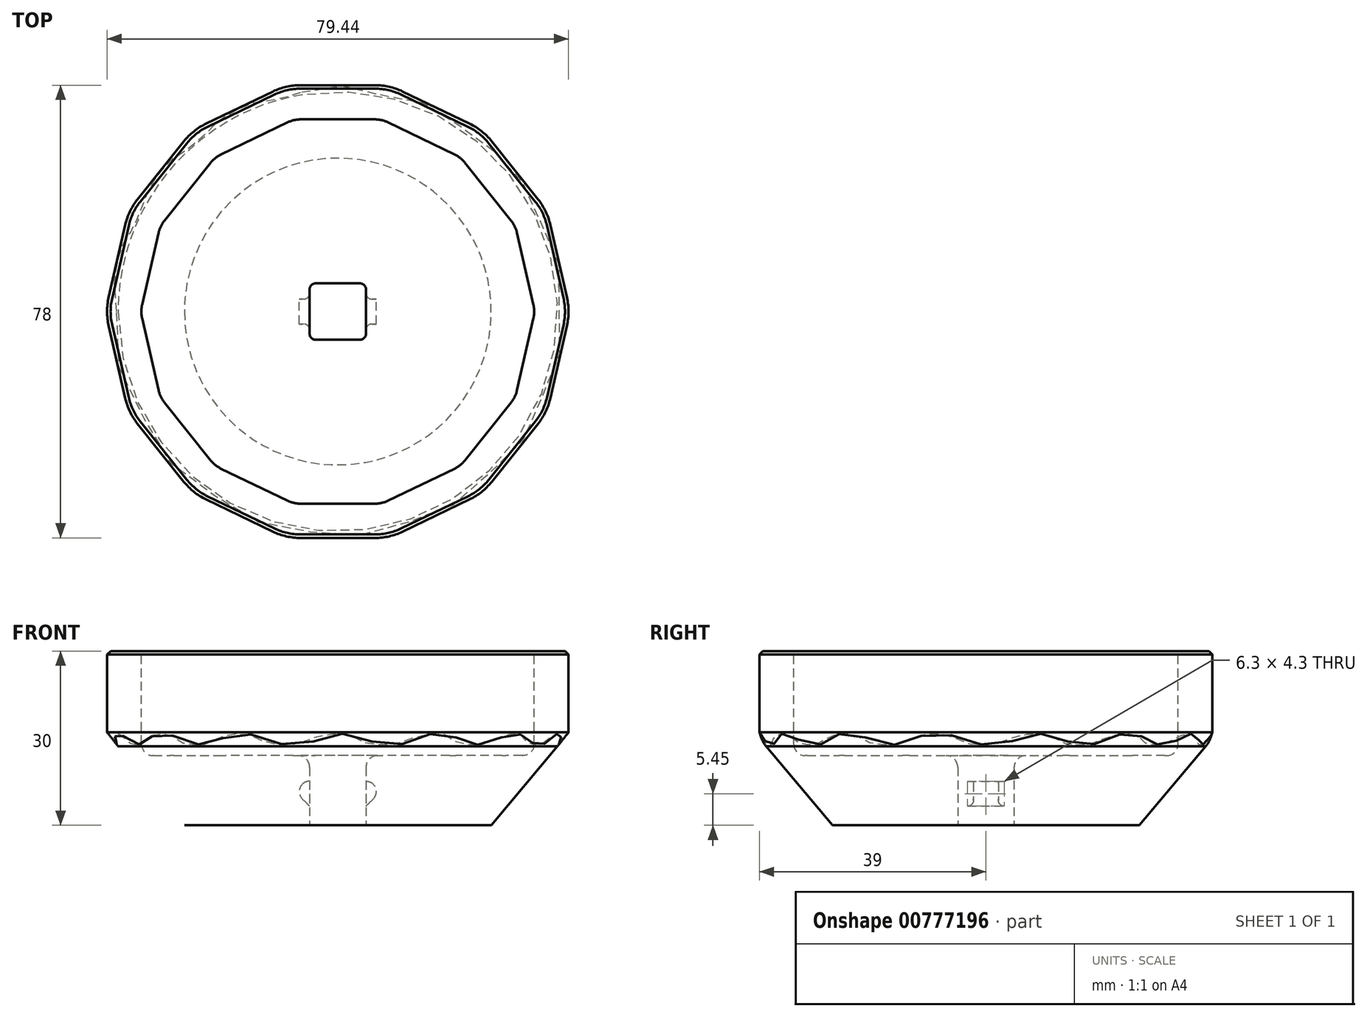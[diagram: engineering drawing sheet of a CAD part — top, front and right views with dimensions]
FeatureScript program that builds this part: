
annotation { "Feature Type Name" : "Feature", "Feature Type Description" : "" }
export const myFeature = defineFeature(function(context is Context, id is Id, definition is map)
    precondition{}
    {
        {
            var Q0;
            Q0=qCreatedBy(makeId("Top.planeOp"),FACE);
            var sketch = newSketch(context, id + "F0", { "sketchPlane" : qUnion([Q0])});
            skLineSegment(sketch, "E0.bottom", {"start": v(3.85, 4.85) * mm, "end": v(-3.85, 4.85) * mm});
            skLineSegment(sketch, "E0.top", {"start": v(3.85, -4.85) * mm, "end": v(-3.85, -4.85) * mm});
            skLineSegment(sketch, "E0.left", {"start": v(4.85, 3.85) * mm, "end": v(4.85, -3.85) * mm});
            skLineSegment(sketch, "E0.right", {"start": v(-4.85, 3.85) * mm, "end": v(-4.85, -3.85) * mm});
            skPoint(sketch, "E0.middle", {"position": v(0, 0) * mm});
            skPoint(sketch, "E1.visualSharp", {"position": v(-4.85, -4.85) * mm});
            skArc(sketch, "E1.filletArc", {"start": v(-4.85, -3.85) * mm, "mid": v(-4.56, -4.56) * mm, "end": v(-3.85, -4.85) * mm});
            skPoint(sketch, "E2.visualSharp", {"position": v(4.85, -4.85) * mm});
            skArc(sketch, "E2.filletArc", {"start": v(3.85, -4.85) * mm, "mid": v(4.56, -4.56) * mm, "end": v(4.85, -3.85) * mm});
            skPoint(sketch, "E3.visualSharp", {"position": v(4.85, 4.85) * mm});
            skArc(sketch, "E3.filletArc", {"start": v(4.85, 3.85) * mm, "mid": v(4.56, 4.56) * mm, "end": v(3.85, 4.85) * mm});
            skPoint(sketch, "E4.visualSharp", {"position": v(-4.85, 4.85) * mm});
            skArc(sketch, "E4.filletArc", {"start": v(-3.85, 4.85) * mm, "mid": v(-4.56, 4.56) * mm, "end": v(-4.85, 3.85) * mm});
            skSolve(sketch);
        }
        {
            var Q0;
            Q0=qCreatedBy(makeId("Front.planeOp"),FACE);
            var sketch = newSketch(context, id + "F1", { "sketchPlane" : qUnion([Q0])});
            skLineSegment(sketch, "E5", {"start": v(0, 0) * mm, "end": v(0, 30) * mm});
            skLineSegment(sketch, "E6", {"start": v(0, 30) * mm, "end": v(-39, 30) * mm});
            skLineSegment(sketch, "E7", {"start": v(-39, 30) * mm, "end": v(-39, 16.82) * mm});
            skLineSegment(sketch, "E8", {"start": v(-37.83, 13.6) * mm, "end": v(-26.41, 0) * mm});
            skLineSegment(sketch, "E9", {"start": v(-26.41, 0) * mm, "end": v(0, 0) * mm});
            skLineSegment(sketch, "E10", {"start": v(0, 0) * mm, "end": v(0, -5.87) * mm, "construction": true});
            skPoint(sketch, "E11.visualSharp", {"position": v(-39, 15) * mm});
            skArc(sketch, "E11.filletArc", {"start": v(-39, 16.82) * mm, "mid": v(-38.7, 15.1) * mm, "end": v(-37.83, 13.6) * mm});
            skSolve(sketch);
        }
        {
            var Q0;
            Q0 = qSketchRegion(id + "F1", true);
            var Q1;
            Q1=sQuery(id+"F1.wireOp",EDGE,"E5");
            revolve(context, id + "F2", {"surfaceOperationType" : NewSurfaceOperationType.NEW, "entities" : qUnion([Q0]), "axis" : qUnion([Q1]), "revolveType" : RevolveType.FULL});
        }
        {
            var Q0;
            Q0 = qSketchRegion(id + "F0", true);
            extrude(context, id + "F3", {"entities" : qUnion([Q0]), "operationType" : NewBodyOperationType.REMOVE, "endBound" : BoundingType.THROUGH_ALL, "depth" : 12 * mm, "offsetDistance" : 25 * mm});
        }
        {
            var Q0;
            Q0=makeQuery(id+"F2.opRevolve","SWEPT_FACE",FACE,{"disambiguationData":[OSD([sQuery(id+"F1.wireOp",EDGE,"E6")])]});
            var sketch = newSketch(context, id + "F4", { "sketchPlane" : qUnion([Q0])});
            skCircle(sketch, "E12.cCircle", {"center": v(0, 0) * mm, "radius": 33.95 * mm, "construction": true});
            skLineSegment(sketch, "E12.0", {"start": v(21.88, 25.65) * mm, "end": v(29.88, 15.62) * mm});
            skLineSegment(sketch, "E12.1", {"start": v(30.84, 13.62) * mm, "end": v(33.7, 1.11) * mm});
            skLineSegment(sketch, "E12.2", {"start": v(33.7, -1.11) * mm, "end": v(30.84, -13.62) * mm});
            skLineSegment(sketch, "E12.3", {"start": v(29.88, -15.62) * mm, "end": v(21.88, -25.65) * mm});
            skLineSegment(sketch, "E12.4", {"start": v(20.14, -27.04) * mm, "end": v(8.58, -32.6) * mm});
            skLineSegment(sketch, "E12.5", {"start": v(6.41, -33.1) * mm, "end": v(-6.41, -33.1) * mm});
            skLineSegment(sketch, "E12.6", {"start": v(-8.58, -32.6) * mm, "end": v(-20.14, -27.04) * mm});
            skLineSegment(sketch, "E12.7", {"start": v(-21.88, -25.65) * mm, "end": v(-29.88, -15.62) * mm});
            skLineSegment(sketch, "E12.8", {"start": v(-30.84, -13.62) * mm, "end": v(-33.7, -1.11) * mm});
            skLineSegment(sketch, "E12.9", {"start": v(-33.7, 1.11) * mm, "end": v(-30.84, 13.62) * mm});
            skLineSegment(sketch, "E12.10", {"start": v(-29.88, 15.62) * mm, "end": v(-21.88, 25.65) * mm});
            skLineSegment(sketch, "E12.11", {"start": v(-20.14, 27.04) * mm, "end": v(-8.58, 32.6) * mm});
            skLineSegment(sketch, "E12.12", {"start": v(-6.41, 33.1) * mm, "end": v(6.41, 33.1) * mm});
            skLineSegment(sketch, "E12.13", {"start": v(8.58, 32.6) * mm, "end": v(20.14, 27.04) * mm});
            skPoint(sketch, "E13.visualSharp", {"position": v(33.95, 0) * mm});
            skArc(sketch, "E13.filletArc", {"start": v(33.7, -1.11) * mm, "mid": v(33.82, 0) * mm, "end": v(33.7, 1.11) * mm});
            skPoint(sketch, "E14.visualSharp", {"position": v(30.59, -14.73) * mm});
            skArc(sketch, "E14.filletArc", {"start": v(29.88, -15.62) * mm, "mid": v(30.47, -14.68) * mm, "end": v(30.84, -13.62) * mm});
            skPoint(sketch, "E15.visualSharp", {"position": v(30.59, 14.73) * mm});
            skArc(sketch, "E15.filletArc", {"start": v(30.84, 13.62) * mm, "mid": v(30.47, 14.68) * mm, "end": v(29.88, 15.62) * mm});
            skPoint(sketch, "E16.visualSharp", {"position": v(21.17, 26.54) * mm});
            skArc(sketch, "E16.filletArc", {"start": v(21.88, 25.65) * mm, "mid": v(21.09, 26.44) * mm, "end": v(20.14, 27.04) * mm});
            skPoint(sketch, "E17.visualSharp", {"position": v(7.55, 33.1) * mm});
            skArc(sketch, "E17.filletArc", {"start": v(8.58, 32.6) * mm, "mid": v(7.53, 32.97) * mm, "end": v(6.41, 33.1) * mm});
            skPoint(sketch, "E18.visualSharp", {"position": v(-7.55, 33.1) * mm});
            skArc(sketch, "E18.filletArc", {"start": v(-6.41, 33.1) * mm, "mid": v(-7.53, 32.97) * mm, "end": v(-8.58, 32.6) * mm});
            skPoint(sketch, "E19.visualSharp", {"position": v(-21.17, 26.54) * mm});
            skArc(sketch, "E19.filletArc", {"start": v(-20.14, 27.04) * mm, "mid": v(-21.09, 26.44) * mm, "end": v(-21.88, 25.65) * mm});
            skPoint(sketch, "E20.visualSharp", {"position": v(-30.59, 14.73) * mm});
            skArc(sketch, "E20.filletArc", {"start": v(-29.88, 15.62) * mm, "mid": v(-30.47, 14.68) * mm, "end": v(-30.84, 13.62) * mm});
            skPoint(sketch, "E21.visualSharp", {"position": v(-33.95, 0) * mm});
            skArc(sketch, "E21.filletArc", {"start": v(-33.7, 1.11) * mm, "mid": v(-33.82, 0) * mm, "end": v(-33.7, -1.11) * mm});
            skPoint(sketch, "E22.visualSharp", {"position": v(-30.59, -14.73) * mm});
            skArc(sketch, "E22.filletArc", {"start": v(-30.84, -13.62) * mm, "mid": v(-30.47, -14.68) * mm, "end": v(-29.88, -15.62) * mm});
            skPoint(sketch, "E23.visualSharp", {"position": v(-21.17, -26.54) * mm});
            skArc(sketch, "E23.filletArc", {"start": v(-21.88, -25.65) * mm, "mid": v(-21.09, -26.44) * mm, "end": v(-20.14, -27.04) * mm});
            skPoint(sketch, "E24.visualSharp", {"position": v(-7.55, -33.1) * mm});
            skArc(sketch, "E24.filletArc", {"start": v(-8.58, -32.6) * mm, "mid": v(-7.53, -32.97) * mm, "end": v(-6.41, -33.1) * mm});
            skPoint(sketch, "E25.visualSharp", {"position": v(7.55, -33.1) * mm});
            skArc(sketch, "E25.filletArc", {"start": v(6.41, -33.1) * mm, "mid": v(7.53, -32.97) * mm, "end": v(8.58, -32.6) * mm});
            skPoint(sketch, "E26.visualSharp", {"position": v(21.17, -26.54) * mm});
            skArc(sketch, "E26.filletArc", {"start": v(20.14, -27.04) * mm, "mid": v(21.09, -26.44) * mm, "end": v(21.88, -25.65) * mm});
            skSolve(sketch);
        }
        {
            var Q0;
            Q0=makeQuery(id+"F4.imprint","IMPRINT",FACE,{"disambiguationData":[TD([[makeQuery(id+"F4.imprint","IMPRINT",EDGE,{"derivedFrom":sQuery(id+"F4.wireOp",EDGE,"E12.0")}),1.0]])]});
            var sketch = newSketch(context, id + "F5", { "sketchPlane" : qUnion([Q0])});
            skCircle(sketch, "E27.0", {"center": v(0, 0) * mm, "radius": 33.95 * mm, "construction": true});
            skLineSegment(sketch, "E27.1", {"start": v(21.88, 25.65) * mm, "end": v(29.88, 15.62) * mm});
            skLineSegment(sketch, "E27.2", {"start": v(30.84, 13.62) * mm, "end": v(33.7, 1.11) * mm});
            skLineSegment(sketch, "E27.3", {"start": v(33.7, -1.11) * mm, "end": v(30.84, -13.62) * mm});
            skLineSegment(sketch, "E27.4", {"start": v(29.88, -15.62) * mm, "end": v(21.88, -25.65) * mm});
            skLineSegment(sketch, "E27.5", {"start": v(20.14, -27.04) * mm, "end": v(8.58, -32.6) * mm});
            skLineSegment(sketch, "E27.6", {"start": v(6.41, -33.1) * mm, "end": v(-6.41, -33.1) * mm});
            skLineSegment(sketch, "E27.7", {"start": v(-8.58, -32.6) * mm, "end": v(-20.14, -27.04) * mm});
            skLineSegment(sketch, "E27.8", {"start": v(-21.88, -25.65) * mm, "end": v(-29.88, -15.62) * mm});
            skLineSegment(sketch, "E27.9", {"start": v(-30.84, -13.62) * mm, "end": v(-33.7, -1.11) * mm});
            skLineSegment(sketch, "E27.10", {"start": v(-33.7, 1.11) * mm, "end": v(-30.84, 13.62) * mm});
            skLineSegment(sketch, "E27.11", {"start": v(-29.88, 15.62) * mm, "end": v(-21.88, 25.65) * mm});
            skLineSegment(sketch, "E27.12", {"start": v(-20.14, 27.04) * mm, "end": v(-8.58, 32.6) * mm});
            skLineSegment(sketch, "E27.13", {"start": v(-6.41, 33.1) * mm, "end": v(6.41, 33.1) * mm});
            skLineSegment(sketch, "E27.14", {"start": v(8.58, 32.6) * mm, "end": v(20.14, 27.04) * mm});
            skPoint(sketch, "E27.15", {"position": v(33.95, 0) * mm});
            skArc(sketch, "E27.16", {"start": v(33.7, -1.11) * mm, "mid": v(33.82, 0) * mm, "end": v(33.7, 1.11) * mm});
            skPoint(sketch, "E27.17", {"position": v(30.59, -14.73) * mm});
            skArc(sketch, "E27.18", {"start": v(29.88, -15.62) * mm, "mid": v(30.47, -14.68) * mm, "end": v(30.84, -13.62) * mm});
            skPoint(sketch, "E27.19", {"position": v(30.59, 14.73) * mm});
            skArc(sketch, "E27.20", {"start": v(30.84, 13.62) * mm, "mid": v(30.47, 14.68) * mm, "end": v(29.88, 15.62) * mm});
            skPoint(sketch, "E27.21", {"position": v(21.17, 26.54) * mm});
            skArc(sketch, "E27.22", {"start": v(21.88, 25.65) * mm, "mid": v(21.09, 26.44) * mm, "end": v(20.14, 27.04) * mm});
            skPoint(sketch, "E27.23", {"position": v(7.55, 33.1) * mm});
            skArc(sketch, "E27.24", {"start": v(8.58, 32.6) * mm, "mid": v(7.53, 32.97) * mm, "end": v(6.41, 33.1) * mm});
            skPoint(sketch, "E27.25", {"position": v(-7.55, 33.1) * mm});
            skArc(sketch, "E27.26", {"start": v(-6.41, 33.1) * mm, "mid": v(-7.53, 32.97) * mm, "end": v(-8.58, 32.6) * mm});
            skPoint(sketch, "E27.27", {"position": v(-21.17, 26.54) * mm});
            skArc(sketch, "E27.28", {"start": v(-20.14, 27.04) * mm, "mid": v(-21.09, 26.44) * mm, "end": v(-21.88, 25.65) * mm});
            skPoint(sketch, "E27.29", {"position": v(-30.59, 14.73) * mm});
            skArc(sketch, "E27.30", {"start": v(-29.88, 15.62) * mm, "mid": v(-30.47, 14.68) * mm, "end": v(-30.84, 13.62) * mm});
            skPoint(sketch, "E27.31", {"position": v(-33.95, 0) * mm});
            skArc(sketch, "E27.32", {"start": v(-33.7, 1.11) * mm, "mid": v(-33.82, 0) * mm, "end": v(-33.7, -1.11) * mm});
            skPoint(sketch, "E27.33", {"position": v(-30.59, -14.73) * mm});
            skArc(sketch, "E27.34", {"start": v(-30.84, -13.62) * mm, "mid": v(-30.47, -14.68) * mm, "end": v(-29.88, -15.62) * mm});
            skPoint(sketch, "E27.35", {"position": v(-21.17, -26.54) * mm});
            skArc(sketch, "E27.36", {"start": v(-21.88, -25.65) * mm, "mid": v(-21.09, -26.44) * mm, "end": v(-20.14, -27.04) * mm});
            skPoint(sketch, "E27.37", {"position": v(-7.55, -33.1) * mm});
            skArc(sketch, "E27.38", {"start": v(-8.58, -32.6) * mm, "mid": v(-7.53, -32.97) * mm, "end": v(-6.41, -33.1) * mm});
            skPoint(sketch, "E27.39", {"position": v(7.55, -33.1) * mm});
            skArc(sketch, "E27.40", {"start": v(6.41, -33.1) * mm, "mid": v(7.53, -32.97) * mm, "end": v(8.58, -32.6) * mm});
            skPoint(sketch, "E27.41", {"position": v(21.17, -26.54) * mm});
            skArc(sketch, "E27.42", {"start": v(20.14, -27.04) * mm, "mid": v(21.09, -26.44) * mm, "end": v(21.88, -25.65) * mm});
            skArc(sketch, "E28.0", {"start": v(-6.41, 39) * mm, "mid": v(-8.84, 38.73) * mm, "end": v(-11.14, 37.92) * mm});
            skLineSegment(sketch, "E28.1", {"start": v(-22.7, 32.36) * mm, "end": v(-11.14, 37.92) * mm});
            skArc(sketch, "E28.2", {"start": v(-22.7, 32.36) * mm, "mid": v(-24.77, 31.06) * mm, "end": v(-26.5, 29.33) * mm});
            skLineSegment(sketch, "E28.3", {"start": v(-34.5, 19.3) * mm, "end": v(-26.5, 29.33) * mm});
            skArc(sketch, "E28.4", {"start": v(-34.5, 19.3) * mm, "mid": v(-35.79, 17.24) * mm, "end": v(-36.6, 14.93) * mm});
            skLineSegment(sketch, "E28.5", {"start": v(34.5, -19.3) * mm, "end": v(26.5, -29.33) * mm});
            skArc(sketch, "E28.6", {"start": v(34.5, -19.3) * mm, "mid": v(35.79, -17.24) * mm, "end": v(36.6, -14.93) * mm});
            skLineSegment(sketch, "E28.7", {"start": v(39.45, -2.43) * mm, "end": v(36.6, -14.93) * mm});
            skArc(sketch, "E28.8", {"start": v(39.45, -2.43) * mm, "mid": v(39.72, 0) * mm, "end": v(39.45, 2.43) * mm});
            skLineSegment(sketch, "E28.9", {"start": v(36.6, 14.93) * mm, "end": v(39.45, 2.43) * mm});
            skArc(sketch, "E28.10", {"start": v(36.6, 14.93) * mm, "mid": v(35.79, 17.24) * mm, "end": v(34.5, 19.3) * mm});
            skArc(sketch, "E28.11", {"start": v(11.14, 37.92) * mm, "mid": v(8.84, 38.73) * mm, "end": v(6.41, 39) * mm});
            skLineSegment(sketch, "E28.12", {"start": v(11.14, 37.92) * mm, "end": v(22.7, 32.36) * mm});
            skArc(sketch, "E28.13", {"start": v(26.5, 29.33) * mm, "mid": v(24.77, 31.06) * mm, "end": v(22.7, 32.36) * mm});
            skLineSegment(sketch, "E28.14", {"start": v(26.5, 29.33) * mm, "end": v(34.5, 19.3) * mm});
            skArc(sketch, "E28.15", {"start": v(22.7, -32.36) * mm, "mid": v(24.77, -31.06) * mm, "end": v(26.5, -29.33) * mm});
            skLineSegment(sketch, "E28.16", {"start": v(22.7, -32.36) * mm, "end": v(11.14, -37.92) * mm});
            skArc(sketch, "E28.17", {"start": v(6.41, -39) * mm, "mid": v(8.84, -38.73) * mm, "end": v(11.14, -37.92) * mm});
            skLineSegment(sketch, "E28.18", {"start": v(6.41, -39) * mm, "end": v(-6.41, -39) * mm});
            skArc(sketch, "E28.19", {"start": v(-11.14, -37.92) * mm, "mid": v(-8.84, -38.73) * mm, "end": v(-6.41, -39) * mm});
            skLineSegment(sketch, "E28.20", {"start": v(-6.41, 39) * mm, "end": v(6.41, 39) * mm});
            skLineSegment(sketch, "E28.21", {"start": v(-11.14, -37.92) * mm, "end": v(-22.7, -32.36) * mm});
            skArc(sketch, "E28.22", {"start": v(-26.5, -29.33) * mm, "mid": v(-24.77, -31.06) * mm, "end": v(-22.7, -32.36) * mm});
            skLineSegment(sketch, "E28.23", {"start": v(-26.5, -29.33) * mm, "end": v(-34.5, -19.3) * mm});
            skArc(sketch, "E28.24", {"start": v(-36.6, -14.93) * mm, "mid": v(-35.79, -17.24) * mm, "end": v(-34.5, -19.3) * mm});
            skLineSegment(sketch, "E28.25", {"start": v(-36.6, -14.93) * mm, "end": v(-39.45, -2.43) * mm});
            skArc(sketch, "E28.26", {"start": v(-39.45, 2.43) * mm, "mid": v(-39.72, 0) * mm, "end": v(-39.45, -2.43) * mm});
            skLineSegment(sketch, "E28.27", {"start": v(-39.45, 2.43) * mm, "end": v(-36.6, 14.93) * mm});
            skSolve(sketch);
        }
        {
            var Q0;
            Q0=qCreatedBy(makeId("Top.planeOp"),FACE);
            var Q1;
            Q1=sQuery(id+"F1.wireOp",VERTEX,"E8.start");
            cPlane(context, id + "F6", {"entities" : qUnion([Q0, Q1]), "cplaneType" : CPlaneType.PLANE_POINT, "offset" : 25 * mm, "width" : 150 * mm, "height" : 150 * mm});
        }
        {
            var Q0;
            Q0 = qSketchRegion(id + "F5", true);
            var Q1;
            Q1=makeQuery(id+"F11.boolean.opBoolean","COPY",FACE,{"derivedFrom":makeQuery(id+"F11.opExtrude","CAP_FACE",FACE,{"disambiguationData":[OSD([sQuery(id+"F4.wireOp",EDGE,"E12.0"),sQuery(id+"F4.wireOp",EDGE,"E12.1"),sQuery(id+"F4.wireOp",EDGE,"E12.2"),sQuery(id+"F4.wireOp",EDGE,"E12.3"),sQuery(id+"F4.wireOp",EDGE,"E12.4"),sQuery(id+"F4.wireOp",EDGE,"E12.5"),sQuery(id+"F4.wireOp",EDGE,"E12.6"),sQuery(id+"F4.wireOp",EDGE,"E12.7"),sQuery(id+"F4.wireOp",EDGE,"E12.8"),sQuery(id+"F4.wireOp",EDGE,"E12.9"),sQuery(id+"F4.wireOp",EDGE,"E12.10"),sQuery(id+"F4.wireOp",EDGE,"E12.11"),sQuery(id+"F4.wireOp",EDGE,"E12.12"),sQuery(id+"F4.wireOp",EDGE,"E12.13"),sQuery(id+"F4.wireOp",EDGE,"E13.filletArc"),sQuery(id+"F4.wireOp",EDGE,"E14.filletArc"),sQuery(id+"F4.wireOp",EDGE,"E15.filletArc"),sQuery(id+"F4.wireOp",EDGE,"E16.filletArc"),sQuery(id+"F4.wireOp",EDGE,"E17.filletArc"),sQuery(id+"F4.wireOp",EDGE,"E18.filletArc"),sQuery(id+"F4.wireOp",EDGE,"E19.filletArc"),sQuery(id+"F4.wireOp",EDGE,"E20.filletArc"),sQuery(id+"F4.wireOp",EDGE,"E21.filletArc"),sQuery(id+"F4.wireOp",EDGE,"E22.filletArc"),sQuery(id+"F4.wireOp",EDGE,"E23.filletArc"),sQuery(id+"F4.wireOp",EDGE,"E24.filletArc"),sQuery(id+"F4.wireOp",EDGE,"E25.filletArc"),sQuery(id+"F4.wireOp",EDGE,"E26.filletArc")])],"isStart":false})});
            extrude(context, id + "F7", {"entities" : qUnion([Q0]), "operationType" : NewBodyOperationType.ADD, "oppositeDirection" : true, "depth" : 14 * mm, "endBoundEntityFace" : qUnion([Q1]), "offsetDistance" : 25 * mm});
        }
        {
            var Q0;
            Q0=qCreatedBy(id+"F6.planeOp",FACE);
            var sketch = newSketch(context, id + "F8", { "sketchPlane" : qUnion([Q0])});
            skCircle(sketch, "E29.0", {"center": v(0, 0) * mm, "radius": 37.83 * mm});
            skLineSegment(sketch, "E30", {"start": v(6.41, 39) * mm, "end": v(0, 0) * mm, "construction": true});
            skLineSegment(sketch, "E31", {"start": v(0, 0) * mm, "end": v(11.14, 37.92) * mm, "construction": true});
            skPoint(sketch, "E32.0", {"position": v(11.14, 37.92) * mm});
            skPoint(sketch, "E33.1", {"position": v(6.41, 39) * mm});
            skPoint(sketch, "E34", {"position": v(10.67, 36.3) * mm});
            skPoint(sketch, "E35", {"position": v(6.14, 37.33) * mm});
            skPoint(sketch, "E36.1.0", {"position": v(-6.14, 37.33) * mm});
            skPoint(sketch, "E36.1.1", {"position": v(-10.67, 36.3) * mm});
            skPoint(sketch, "E36.2.0", {"position": v(-21.73, 30.97) * mm});
            skPoint(sketch, "E36.2.1", {"position": v(-25.36, 28.07) * mm});
            skPoint(sketch, "E36.3.0", {"position": v(-33.01, 18.47) * mm});
            skPoint(sketch, "E36.3.1", {"position": v(-35.03, 14.3) * mm});
            skPoint(sketch, "E36.4.0", {"position": v(-37.76, 2.32) * mm});
            skPoint(sketch, "E36.4.1", {"position": v(-37.76, -2.32) * mm});
            skPoint(sketch, "E36.5.0", {"position": v(-35.03, -14.3) * mm});
            skPoint(sketch, "E36.5.1", {"position": v(-33.01, -18.47) * mm});
            skPoint(sketch, "E36.6.0", {"position": v(-25.36, -28.07) * mm});
            skPoint(sketch, "E36.6.1", {"position": v(-21.73, -30.97) * mm});
            skPoint(sketch, "E36.7.0", {"position": v(-10.67, -36.3) * mm});
            skPoint(sketch, "E36.7.1", {"position": v(-6.14, -37.33) * mm});
            skPoint(sketch, "E36.8.0", {"position": v(6.14, -37.33) * mm});
            skPoint(sketch, "E36.8.1", {"position": v(10.67, -36.3) * mm});
            skPoint(sketch, "E36.9.0", {"position": v(21.73, -30.97) * mm});
            skPoint(sketch, "E36.9.1", {"position": v(25.36, -28.07) * mm});
            skPoint(sketch, "E36.10.0", {"position": v(33.01, -18.47) * mm});
            skPoint(sketch, "E36.10.1", {"position": v(35.03, -14.3) * mm});
            skPoint(sketch, "E36.11.0", {"position": v(37.76, -2.32) * mm});
            skPoint(sketch, "E36.11.1", {"position": v(37.76, 2.32) * mm});
            skPoint(sketch, "E36.12.0", {"position": v(35.03, 14.3) * mm});
            skPoint(sketch, "E36.12.1", {"position": v(33.01, 18.47) * mm});
            skPoint(sketch, "E36.13.0", {"position": v(25.36, 28.07) * mm});
            skPoint(sketch, "E36.13.1", {"position": v(21.73, 30.97) * mm});
            skSolve(sketch);
        }
        {
            var Q0;
            Q0=makeQuery(id+"F7.opExtrude","CAP_FACE",FACE,{"disambiguationData":[OSD([sQuery(id+"F5.wireOp",EDGE,"E27.1"),sQuery(id+"F5.wireOp",EDGE,"E27.2"),sQuery(id+"F5.wireOp",EDGE,"E27.3"),sQuery(id+"F5.wireOp",EDGE,"E27.4"),sQuery(id+"F5.wireOp",EDGE,"E27.5"),sQuery(id+"F5.wireOp",EDGE,"E27.6"),sQuery(id+"F5.wireOp",EDGE,"E27.7"),sQuery(id+"F5.wireOp",EDGE,"E27.8"),sQuery(id+"F5.wireOp",EDGE,"E27.9"),sQuery(id+"F5.wireOp",EDGE,"E27.10"),sQuery(id+"F5.wireOp",EDGE,"E27.11"),sQuery(id+"F5.wireOp",EDGE,"E27.12"),sQuery(id+"F5.wireOp",EDGE,"E27.13"),sQuery(id+"F5.wireOp",EDGE,"E27.14"),sQuery(id+"F5.wireOp",EDGE,"E27.16"),sQuery(id+"F5.wireOp",EDGE,"E27.18"),sQuery(id+"F5.wireOp",EDGE,"E27.20"),sQuery(id+"F5.wireOp",EDGE,"E27.22"),sQuery(id+"F5.wireOp",EDGE,"E27.24"),sQuery(id+"F5.wireOp",EDGE,"E27.26"),sQuery(id+"F5.wireOp",EDGE,"E27.28"),sQuery(id+"F5.wireOp",EDGE,"E27.30"),sQuery(id+"F5.wireOp",EDGE,"E27.32"),sQuery(id+"F5.wireOp",EDGE,"E27.34"),sQuery(id+"F5.wireOp",EDGE,"E27.36"),sQuery(id+"F5.wireOp",EDGE,"E27.38"),sQuery(id+"F5.wireOp",EDGE,"E27.40"),sQuery(id+"F5.wireOp",EDGE,"E27.42"),sQuery(id+"F5.wireOp",EDGE,"E28.0"),sQuery(id+"F5.wireOp",EDGE,"E28.1"),sQuery(id+"F5.wireOp",EDGE,"E28.2"),sQuery(id+"F5.wireOp",EDGE,"E28.3"),sQuery(id+"F5.wireOp",EDGE,"E28.4"),sQuery(id+"F5.wireOp",EDGE,"E28.5"),sQuery(id+"F5.wireOp",EDGE,"E28.6"),sQuery(id+"F5.wireOp",EDGE,"E28.7"),sQuery(id+"F5.wireOp",EDGE,"E28.8"),sQuery(id+"F5.wireOp",EDGE,"E28.9"),sQuery(id+"F5.wireOp",EDGE,"E28.10"),sQuery(id+"F5.wireOp",EDGE,"E28.11"),sQuery(id+"F5.wireOp",EDGE,"E28.12"),sQuery(id+"F5.wireOp",EDGE,"E28.13"),sQuery(id+"F5.wireOp",EDGE,"E28.14"),sQuery(id+"F5.wireOp",EDGE,"E28.15"),sQuery(id+"F5.wireOp",EDGE,"E28.16"),sQuery(id+"F5.wireOp",EDGE,"E28.17"),sQuery(id+"F5.wireOp",EDGE,"E28.18"),sQuery(id+"F5.wireOp",EDGE,"E28.19"),sQuery(id+"F5.wireOp",EDGE,"E28.20"),sQuery(id+"F5.wireOp",EDGE,"E28.21"),sQuery(id+"F5.wireOp",EDGE,"E28.22"),sQuery(id+"F5.wireOp",EDGE,"E28.23"),sQuery(id+"F5.wireOp",EDGE,"E28.24"),sQuery(id+"F5.wireOp",EDGE,"E28.25"),sQuery(id+"F5.wireOp",EDGE,"E28.26"),sQuery(id+"F5.wireOp",EDGE,"E28.27")])],"isStart":false});
            var sketch = newSketch(context, id + "F9", { "sketchPlane" : qUnion([Q0])});
            skArc(sketch, "E37.43", {"start": v(-6.41, -39) * mm, "mid": v(-8.84, -38.73) * mm, "end": v(-11.14, -37.92) * mm});
            skLineSegment(sketch, "E37.44", {"start": v(-22.7, -32.36) * mm, "end": v(-11.14, -37.92) * mm});
            skArc(sketch, "E37.45", {"start": v(-22.7, -32.36) * mm, "mid": v(-24.77, -31.06) * mm, "end": v(-26.5, -29.33) * mm});
            skLineSegment(sketch, "E37.46", {"start": v(-34.5, -19.3) * mm, "end": v(-26.5, -29.33) * mm});
            skArc(sketch, "E37.47", {"start": v(-34.5, -19.3) * mm, "mid": v(-35.79, -17.24) * mm, "end": v(-36.6, -14.93) * mm});
            skLineSegment(sketch, "E37.48", {"start": v(34.5, 19.3) * mm, "end": v(26.5, 29.33) * mm});
            skArc(sketch, "E37.49", {"start": v(34.5, 19.3) * mm, "mid": v(35.79, 17.24) * mm, "end": v(36.6, 14.93) * mm});
            skLineSegment(sketch, "E37.50", {"start": v(39.45, 2.43) * mm, "end": v(36.6, 14.93) * mm});
            skArc(sketch, "E37.51", {"start": v(39.45, 2.43) * mm, "mid": v(39.72, 0) * mm, "end": v(39.45, -2.43) * mm});
            skLineSegment(sketch, "E37.52", {"start": v(36.6, -14.93) * mm, "end": v(39.45, -2.43) * mm});
            skArc(sketch, "E37.53", {"start": v(36.6, -14.93) * mm, "mid": v(35.79, -17.24) * mm, "end": v(34.5, -19.3) * mm});
            skArc(sketch, "E37.54", {"start": v(11.14, -37.92) * mm, "mid": v(8.84, -38.73) * mm, "end": v(6.41, -39) * mm});
            skLineSegment(sketch, "E37.55", {"start": v(11.14, -37.92) * mm, "end": v(22.7, -32.36) * mm});
            skArc(sketch, "E37.56", {"start": v(26.5, -29.33) * mm, "mid": v(24.77, -31.06) * mm, "end": v(22.7, -32.36) * mm});
            skLineSegment(sketch, "E37.57", {"start": v(26.5, -29.33) * mm, "end": v(34.5, -19.3) * mm});
            skArc(sketch, "E37.58", {"start": v(22.7, 32.36) * mm, "mid": v(24.77, 31.06) * mm, "end": v(26.5, 29.33) * mm});
            skLineSegment(sketch, "E37.59", {"start": v(22.7, 32.36) * mm, "end": v(11.14, 37.92) * mm});
            skArc(sketch, "E37.60", {"start": v(6.41, 39) * mm, "mid": v(8.84, 38.73) * mm, "end": v(11.14, 37.92) * mm});
            skLineSegment(sketch, "E37.61", {"start": v(6.41, 39) * mm, "end": v(-6.41, 39) * mm});
            skArc(sketch, "E37.62", {"start": v(-11.14, 37.92) * mm, "mid": v(-8.84, 38.73) * mm, "end": v(-6.41, 39) * mm});
            skLineSegment(sketch, "E37.63", {"start": v(-6.41, -39) * mm, "end": v(6.41, -39) * mm});
            skLineSegment(sketch, "E37.64", {"start": v(-11.14, 37.92) * mm, "end": v(-22.7, 32.36) * mm});
            skArc(sketch, "E37.65", {"start": v(-26.5, 29.33) * mm, "mid": v(-24.77, 31.06) * mm, "end": v(-22.7, 32.36) * mm});
            skLineSegment(sketch, "E37.66", {"start": v(-26.5, 29.33) * mm, "end": v(-34.5, 19.3) * mm});
            skArc(sketch, "E37.67", {"start": v(-36.6, 14.93) * mm, "mid": v(-35.79, 17.24) * mm, "end": v(-34.5, 19.3) * mm});
            skLineSegment(sketch, "E37.68", {"start": v(-36.6, 14.93) * mm, "end": v(-39.45, 2.43) * mm});
            skArc(sketch, "E37.69", {"start": v(-39.45, -2.43) * mm, "mid": v(-39.72, 0) * mm, "end": v(-39.45, 2.43) * mm});
            skLineSegment(sketch, "E37.70", {"start": v(-39.45, -2.43) * mm, "end": v(-36.6, -14.93) * mm});
            skSolve(sketch);
        }
        {
            var Q1;
            Q1 = qSketchRegion(id + "F9", true);
            var Q2;
            Q2 = qSketchRegion(id + "F8", true);
            loft(context, id + "F10", {"operationType" : NewBodyOperationType.ADD, "sheetProfilesArray" : [{ "sheetProfileEntities" : qUnion([Q1]) }, { "sheetProfileEntities" : qUnion([Q2]) }]});
        }
        {
            var Q0;
            Q0 = qSketchRegion(id + "F4", true);
            extrude(context, id + "F11", {"entities" : qUnion([Q0]), "operationType" : NewBodyOperationType.REMOVE, "oppositeDirection" : true, "depth" : 18 * mm, "offsetDistance" : 25 * mm});
        }
        {
            var Q0;
            Q0=qCreatedBy(makeId("Front.planeOp"),FACE);
            var sketch = newSketch(context, id + "F12", { "sketchPlane" : qUnion([Q0])});
            skLineSegment(sketch, "E38", {"start": v(-4.85, 7.6) * mm, "end": v(0, 7.6) * mm});
            skLineSegment(sketch, "E39", {"start": v(-4.85, 3.3) * mm, "end": v(0, 3.3) * mm});
            skLineSegment(sketch, "E40", {"start": v(-5.67, 5.45) * mm, "end": v(-0.86, 5.45) * mm, "construction": true});
            skLineSegment(sketch, "E41", {"start": v(-4.85, 3.3) * mm, "end": v(-6.1, 4.56) * mm});
            skArc(sketch, "E42", {"start": v(-4.85, 7.6) * mm, "mid": v(-6.5, 6.5) * mm, "end": v(-6.1, 4.56) * mm});
            skLineSegment(sketch, "E43.MirrorCS", {"start": v(4.85, 7.6) * mm, "end": v(0, 7.6) * mm});
            skArc(sketch, "E44.MirrorCS", {"start": v(4.85, 7.6) * mm, "mid": v(6.5, 6.5) * mm, "end": v(6.1, 4.56) * mm});
            skLineSegment(sketch, "E45.MirrorCS", {"start": v(4.85, 3.3) * mm, "end": v(6.1, 4.56) * mm});
            skLineSegment(sketch, "E46.MirrorCS", {"start": v(4.85, 3.3) * mm, "end": v(0, 3.3) * mm});
            skLineSegment(sketch, "E47.MirrorCS", {"start": v(5.67, 5.45) * mm, "end": v(0.86, 5.45) * mm, "construction": true});
            skSolve(sketch);
        }
        {
            var Q0;
            Q0 = qSketchRegion(id + "F12", true);
            extrude(context, id + "F13", {"entities" : qUnion([Q0]), "operationType" : NewBodyOperationType.REMOVE, "endBound" : BoundingType.SYMMETRIC, "depth" : 4.3 * mm, "offsetDistance" : 25 * mm});
        }
        {
            var Q0;
            Q0=makeQuery(id+"F13.boolean.opBoolean","INTERSECT",EDGE,{"derivedFrom":[makeQuery(id+"F3.boolean.opBoolean","COPY",FACE,{"derivedFrom":makeQuery(id+"F3.opExtrude","SWEPT_FACE",FACE,{"disambiguationData":[OSD([sQuery(id+"F0.wireOp",EDGE,"E0.right")])]})}),makeQuery(id+"F13.opExtrude","CAP_FACE",FACE,{"disambiguationData":[OSD([sQuery(id+"F12.wireOp",EDGE,"E38"),sQuery(id+"F12.wireOp",EDGE,"E39"),sQuery(id+"F12.wireOp",EDGE,"E41"),sQuery(id+"F12.wireOp",EDGE,"E42"),sQuery(id+"F12.wireOp",EDGE,"E43.MirrorCS"),sQuery(id+"F12.wireOp",EDGE,"E44.MirrorCS"),sQuery(id+"F12.wireOp",EDGE,"E45.MirrorCS"),sQuery(id+"F12.wireOp",EDGE,"E46.MirrorCS")])],"isStart":false})]});
            var Q1;
            Q1=makeQuery(id+"FJ3eJoukwGj3lDz_1.1.F13.boolean.opBoolean","INTERSECT",EDGE,{"derivedFrom":[makeQuery(id+"F3.boolean.opBoolean","COPY",FACE,{"derivedFrom":makeQuery(id+"F3.opExtrude","SWEPT_FACE",FACE,{"disambiguationData":[OSD([sQuery(id+"F0.wireOp",EDGE,"E0.top")])]})}),makeQuery(id+"FJ3eJoukwGj3lDz_1.1.F13.opExtrude","CAP_FACE",FACE,{"disambiguationData":[OSD([sQuery(id+"F12.wireOp",EDGE,"E38"),sQuery(id+"F12.wireOp",EDGE,"E39"),sQuery(id+"F12.wireOp",EDGE,"E41"),sQuery(id+"F12.wireOp",EDGE,"E42"),sQuery(id+"F12.wireOp",EDGE,"E43.MirrorCS"),sQuery(id+"F12.wireOp",EDGE,"E44.MirrorCS"),sQuery(id+"F12.wireOp",EDGE,"E45.MirrorCS"),sQuery(id+"F12.wireOp",EDGE,"E46.MirrorCS")])],"isStart":true})]});
            var Q2;
            Q2=makeQuery(id+"F13.boolean.opBoolean","INTERSECT",EDGE,{"derivedFrom":[makeQuery(id+"F3.boolean.opBoolean","COPY",FACE,{"derivedFrom":makeQuery(id+"F3.opExtrude","SWEPT_FACE",FACE,{"disambiguationData":[OSD([sQuery(id+"F0.wireOp",EDGE,"E0.right")])]})}),makeQuery(id+"F13.opExtrude","CAP_FACE",FACE,{"disambiguationData":[OSD([sQuery(id+"F12.wireOp",EDGE,"E38"),sQuery(id+"F12.wireOp",EDGE,"E39"),sQuery(id+"F12.wireOp",EDGE,"E41"),sQuery(id+"F12.wireOp",EDGE,"E42"),sQuery(id+"F12.wireOp",EDGE,"E43.MirrorCS"),sQuery(id+"F12.wireOp",EDGE,"E44.MirrorCS"),sQuery(id+"F12.wireOp",EDGE,"E45.MirrorCS"),sQuery(id+"F12.wireOp",EDGE,"E46.MirrorCS")])],"isStart":true})]});
            var Q3;
            Q3=makeQuery(id+"FJ3eJoukwGj3lDz_1.1.F13.boolean.opBoolean","INTERSECT",EDGE,{"derivedFrom":[makeQuery(id+"F3.boolean.opBoolean","COPY",FACE,{"derivedFrom":makeQuery(id+"F3.opExtrude","SWEPT_FACE",FACE,{"disambiguationData":[OSD([sQuery(id+"F0.wireOp",EDGE,"E0.bottom")])]})}),makeQuery(id+"FJ3eJoukwGj3lDz_1.1.F13.opExtrude","CAP_FACE",FACE,{"disambiguationData":[OSD([sQuery(id+"F12.wireOp",EDGE,"E38"),sQuery(id+"F12.wireOp",EDGE,"E39"),sQuery(id+"F12.wireOp",EDGE,"E41"),sQuery(id+"F12.wireOp",EDGE,"E42"),sQuery(id+"F12.wireOp",EDGE,"E43.MirrorCS"),sQuery(id+"F12.wireOp",EDGE,"E44.MirrorCS"),sQuery(id+"F12.wireOp",EDGE,"E45.MirrorCS"),sQuery(id+"F12.wireOp",EDGE,"E46.MirrorCS")])],"isStart":true})]});
            var Q4;
            Q4=makeQuery(id+"FJ3eJoukwGj3lDz_1.1.F13.boolean.opBoolean","INTERSECT",EDGE,{"derivedFrom":[makeQuery(id+"F3.boolean.opBoolean","COPY",FACE,{"derivedFrom":makeQuery(id+"F3.opExtrude","SWEPT_FACE",FACE,{"disambiguationData":[OSD([sQuery(id+"F0.wireOp",EDGE,"E0.bottom")])]})}),makeQuery(id+"FJ3eJoukwGj3lDz_1.1.F13.opExtrude","CAP_FACE",FACE,{"disambiguationData":[OSD([sQuery(id+"F12.wireOp",EDGE,"E38"),sQuery(id+"F12.wireOp",EDGE,"E39"),sQuery(id+"F12.wireOp",EDGE,"E41"),sQuery(id+"F12.wireOp",EDGE,"E42"),sQuery(id+"F12.wireOp",EDGE,"E43.MirrorCS"),sQuery(id+"F12.wireOp",EDGE,"E44.MirrorCS"),sQuery(id+"F12.wireOp",EDGE,"E45.MirrorCS"),sQuery(id+"F12.wireOp",EDGE,"E46.MirrorCS")])],"isStart":false})]});
            var Q5;
            Q5=makeQuery(id+"FJ3eJoukwGj3lDz_1.1.F13.boolean.opBoolean","COPY",EDGE,{"derivedFrom":makeQuery(id+"FJ3eJoukwGj3lDz_1.1.F13.opExtrude","SWEPT_EDGE",EDGE,{"disambiguationData":[OSD([sQuery(id+"F12.wireOp",EDGE,"E45.MirrorCS"),sQuery(id+"F12.wireOp",EDGE,"E46.MirrorCS")])]})});
            var Q6;
            Q6=makeQuery(id+"F13.boolean.opBoolean","COPY",EDGE,{"derivedFrom":makeQuery(id+"F13.opExtrude","SWEPT_EDGE",EDGE,{"disambiguationData":[OSD([sQuery(id+"F12.wireOp",EDGE,"E39"),sQuery(id+"F12.wireOp",EDGE,"E41")])]})});
            var Q7;
            Q7=makeQuery(id+"FJ3eJoukwGj3lDz_1.1.F13.boolean.opBoolean","COPY",EDGE,{"derivedFrom":makeQuery(id+"FJ3eJoukwGj3lDz_1.1.F13.opExtrude","SWEPT_EDGE",EDGE,{"disambiguationData":[OSD([sQuery(id+"F12.wireOp",EDGE,"E39"),sQuery(id+"F12.wireOp",EDGE,"E41")])]})});
            var Q8;
            Q8=makeQuery(id+"F13.boolean.opBoolean","COPY",EDGE,{"derivedFrom":makeQuery(id+"F13.opExtrude","SWEPT_EDGE",EDGE,{"disambiguationData":[OSD([sQuery(id+"F12.wireOp",EDGE,"E45.MirrorCS"),sQuery(id+"F12.wireOp",EDGE,"E46.MirrorCS")])]})});
            var Q9;
            Q9=makeQuery(id+"F13.boolean.opBoolean","INTERSECT",EDGE,{"derivedFrom":[makeQuery(id+"F3.boolean.opBoolean","COPY",FACE,{"derivedFrom":makeQuery(id+"F3.opExtrude","SWEPT_FACE",FACE,{"disambiguationData":[OSD([sQuery(id+"F0.wireOp",EDGE,"E0.left")])]})}),makeQuery(id+"F13.opExtrude","CAP_FACE",FACE,{"disambiguationData":[OSD([sQuery(id+"F12.wireOp",EDGE,"E38"),sQuery(id+"F12.wireOp",EDGE,"E39"),sQuery(id+"F12.wireOp",EDGE,"E41"),sQuery(id+"F12.wireOp",EDGE,"E42"),sQuery(id+"F12.wireOp",EDGE,"E43.MirrorCS"),sQuery(id+"F12.wireOp",EDGE,"E44.MirrorCS"),sQuery(id+"F12.wireOp",EDGE,"E45.MirrorCS"),sQuery(id+"F12.wireOp",EDGE,"E46.MirrorCS")])],"isStart":true})]});
            var Q10;
            Q10=makeQuery(id+"F13.boolean.opBoolean","INTERSECT",EDGE,{"derivedFrom":[makeQuery(id+"F3.boolean.opBoolean","COPY",FACE,{"derivedFrom":makeQuery(id+"F3.opExtrude","SWEPT_FACE",FACE,{"disambiguationData":[OSD([sQuery(id+"F0.wireOp",EDGE,"E0.left")])]})}),makeQuery(id+"F13.opExtrude","CAP_FACE",FACE,{"disambiguationData":[OSD([sQuery(id+"F12.wireOp",EDGE,"E38"),sQuery(id+"F12.wireOp",EDGE,"E39"),sQuery(id+"F12.wireOp",EDGE,"E41"),sQuery(id+"F12.wireOp",EDGE,"E42"),sQuery(id+"F12.wireOp",EDGE,"E43.MirrorCS"),sQuery(id+"F12.wireOp",EDGE,"E44.MirrorCS"),sQuery(id+"F12.wireOp",EDGE,"E45.MirrorCS"),sQuery(id+"F12.wireOp",EDGE,"E46.MirrorCS")])],"isStart":false})]});
            fillet(context, id + "F14", {"entities" : qUnion([Q0, Q1, Q2, Q3, Q4, Q5, Q6, Q7, Q8, Q9, Q10]), "radius" : 1 * mm, "tangentPropagation" : true, "allowEdgeOverflow" : false});
        }
        {
            var Q0;
            Q0=makeQuery(id+"F11.boolean.opBoolean","INTERSECT",EDGE,{"derivedFrom":[makeQuery(id+"F3.boolean.opBoolean","COPY",FACE,{"derivedFrom":makeQuery(id+"F3.opExtrude","SWEPT_FACE",FACE,{"disambiguationData":[OSD([sQuery(id+"F0.wireOp",EDGE,"E0.bottom")])]})}),makeQuery(id+"F11.opExtrude","CAP_FACE",FACE,{"disambiguationData":[OSD([sQuery(id+"F4.wireOp",EDGE,"E12.0"),sQuery(id+"F4.wireOp",EDGE,"E12.1"),sQuery(id+"F4.wireOp",EDGE,"E12.2"),sQuery(id+"F4.wireOp",EDGE,"E12.3"),sQuery(id+"F4.wireOp",EDGE,"E12.4"),sQuery(id+"F4.wireOp",EDGE,"E12.5"),sQuery(id+"F4.wireOp",EDGE,"E12.6"),sQuery(id+"F4.wireOp",EDGE,"E12.7"),sQuery(id+"F4.wireOp",EDGE,"E12.8"),sQuery(id+"F4.wireOp",EDGE,"E12.9"),sQuery(id+"F4.wireOp",EDGE,"E12.10"),sQuery(id+"F4.wireOp",EDGE,"E12.11"),sQuery(id+"F4.wireOp",EDGE,"E12.12"),sQuery(id+"F4.wireOp",EDGE,"E12.13"),sQuery(id+"F4.wireOp",EDGE,"E13.filletArc"),sQuery(id+"F4.wireOp",EDGE,"E14.filletArc"),sQuery(id+"F4.wireOp",EDGE,"E15.filletArc"),sQuery(id+"F4.wireOp",EDGE,"E16.filletArc"),sQuery(id+"F4.wireOp",EDGE,"E17.filletArc"),sQuery(id+"F4.wireOp",EDGE,"E18.filletArc"),sQuery(id+"F4.wireOp",EDGE,"E19.filletArc"),sQuery(id+"F4.wireOp",EDGE,"E20.filletArc"),sQuery(id+"F4.wireOp",EDGE,"E21.filletArc"),sQuery(id+"F4.wireOp",EDGE,"E22.filletArc"),sQuery(id+"F4.wireOp",EDGE,"E23.filletArc"),sQuery(id+"F4.wireOp",EDGE,"E24.filletArc"),sQuery(id+"F4.wireOp",EDGE,"E25.filletArc"),sQuery(id+"F4.wireOp",EDGE,"E26.filletArc")])],"isStart":false})]});
            var Q1;
            Q1=makeQuery(id+"F11.boolean.opBoolean","COPY",EDGE,{"derivedFrom":makeQuery(id+"F11.opExtrude","CAP_EDGE",EDGE,{"disambiguationData":[OSD([sQuery(id+"F4.wireOp",EDGE,"E12.10")])],"isStart":false})});
            fillet(context, id + "F15", {"entities" : qUnion([Q0, Q1]), "radius" : 2 * mm, "tangentPropagation" : true, "allowEdgeOverflow" : false});
        }
        {
            var Q0;
            Q0=makeQuery(id+"F3.boolean.opBoolean","COPY",EDGE,{"derivedFrom":makeQuery(id+"F3.opExtrude","CAP_EDGE",EDGE,{"disambiguationData":[OSD([sQuery(id+"F0.wireOp",EDGE,"E0.bottom")])],"isStart":true})});
            var Q1;
            Q1=makeQuery(id+"F11.boolean.opBoolean","COPY",EDGE,{"derivedFrom":makeQuery(id+"F11.opExtrude","CAP_EDGE",EDGE,{"disambiguationData":[OSD([sQuery(id+"F4.wireOp",EDGE,"E12.8")])],"isStart":true})});
            var Q2;
            Q2=makeQuery(id+"F7.opExtrude","CAP_EDGE",EDGE,{"disambiguationData":[OSD([sQuery(id+"F5.wireOp",EDGE,"E28.23")])],"isStart":true});
            chamfer(context, id + "F16", {"entities" : qUnion([Q0, Q1, Q2]), "width" : 0.6 * mm, "tangentPropagation" : true});
        }
    });
